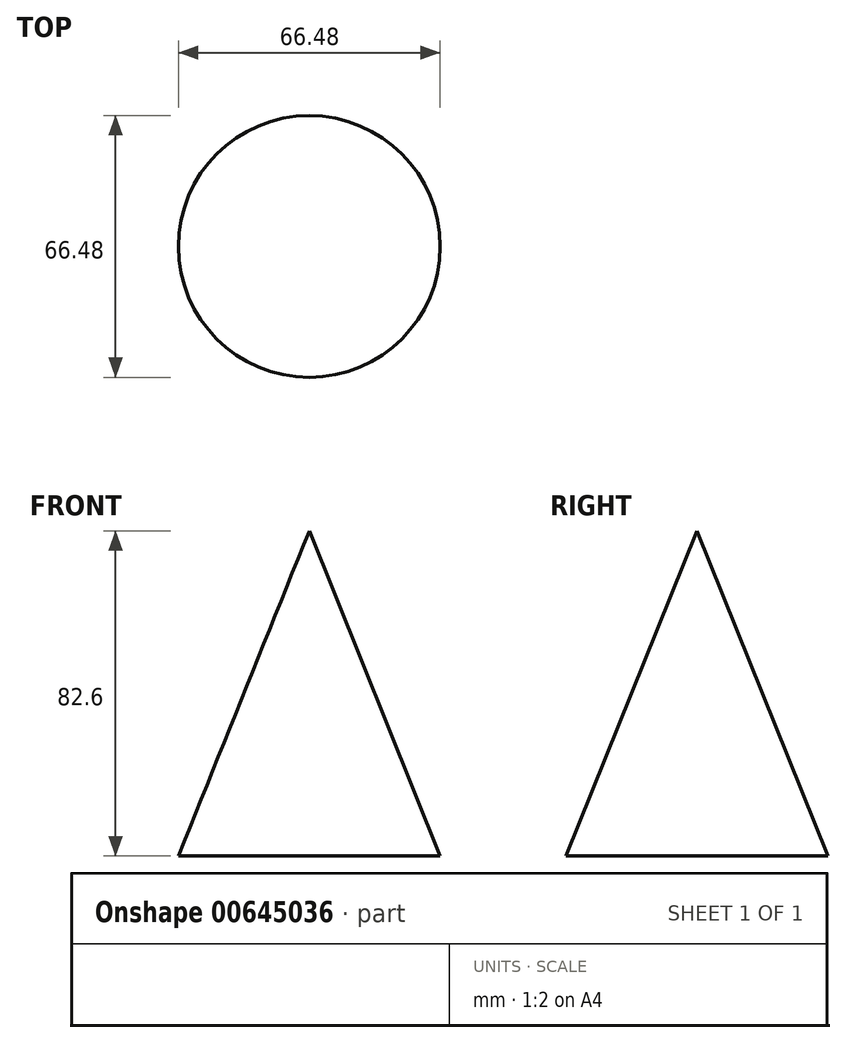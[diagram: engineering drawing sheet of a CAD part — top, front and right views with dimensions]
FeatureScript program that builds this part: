
annotation { "Feature Type Name" : "Feature", "Feature Type Description" : "" }
export const myFeature = defineFeature(function(context is Context, id is Id, definition is map)
    precondition{}
    {
        {
            var Q0;
            Q0=qCreatedBy(makeId("Front.planeOp"),FACE);
            var sketch = newSketch(context, id + "F0", { "sketchPlane" : qUnion([Q0])});
            skLineSegment(sketch, "E0", {"start": v(0, -35.54) * mm, "end": v(0, 47.06) * mm});
            skLineSegment(sketch, "E1", {"start": v(0, 47.06) * mm, "end": v(33.24, -35.54) * mm});
            skLineSegment(sketch, "E2", {"start": v(33.24, -35.54) * mm, "end": v(0, -35.54) * mm});
            skSolve(sketch);
        }
        {
            var Q0;
            Q0=makeQuery(id+"F0.imprint","IMPRINT",FACE,{"disambiguationData":[TD([[makeQuery(id+"F0.imprint","IMPRINT",EDGE,{"derivedFrom":sQuery(id+"F0.wireOp",EDGE,"E0")}),-1.0]])]});
            var Q1;
            Q1=sQuery(id+"F0.wireOp",EDGE,"E0");
            revolve(context, id + "F1", {"entities" : qUnion([Q0]), "axis" : qUnion([Q1]), "revolveType" : RevolveType.FULL});
        }
    });
